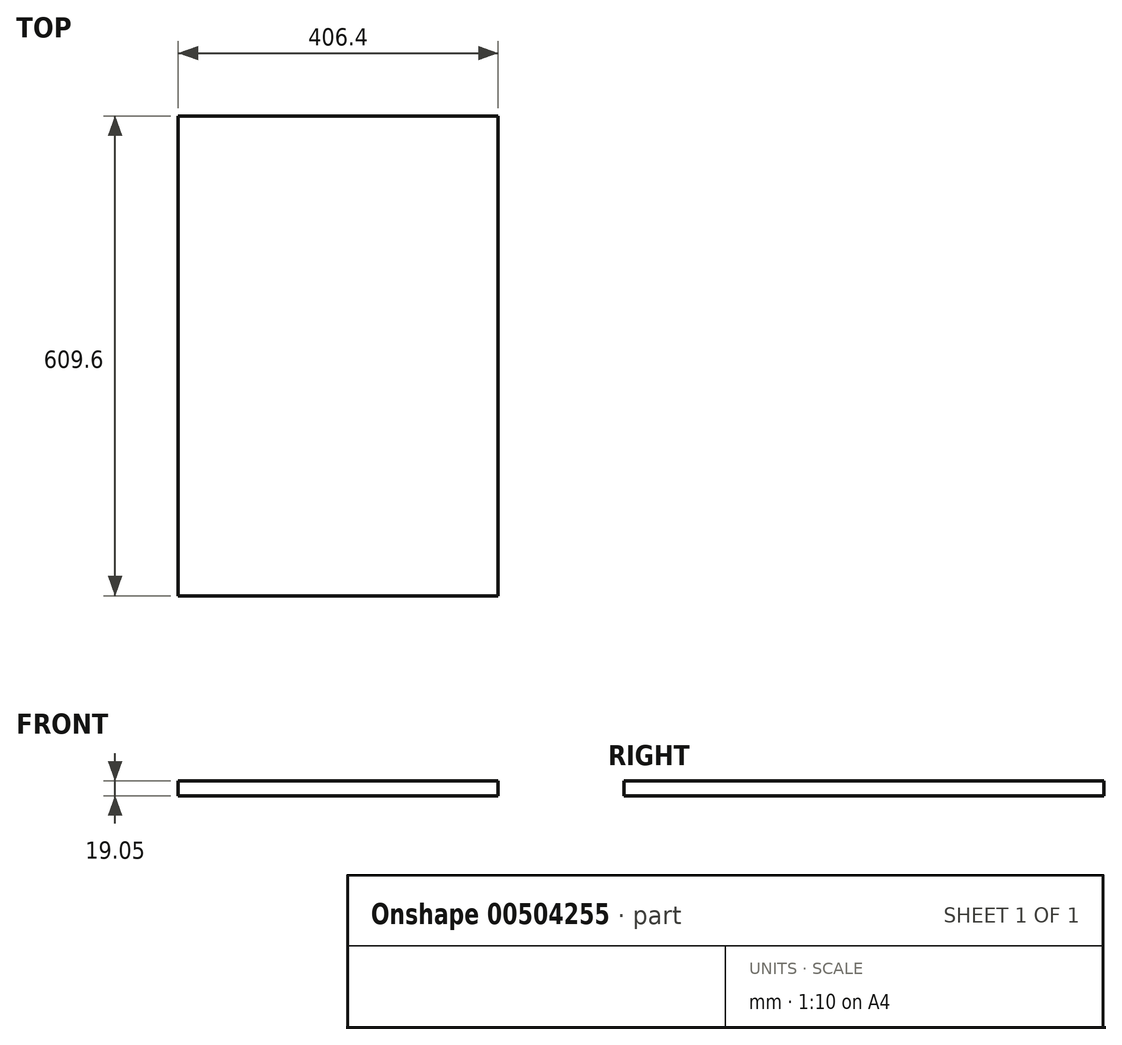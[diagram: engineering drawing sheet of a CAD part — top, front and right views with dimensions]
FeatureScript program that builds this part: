
annotation { "Feature Type Name" : "Feature", "Feature Type Description" : "" }
export const myFeature = defineFeature(function(context is Context, id is Id, definition is map)
    precondition{}
    {
        {
            var Q0;
            Q0=qCreatedBy(makeId("Top.planeOp"),FACE);
            var sketch = newSketch(context, id + "F0", { "sketchPlane" : qUnion([Q0])});
            skLineSegment(sketch, "E0.bottom", {"start": v(203.2, -304.8) * mm, "end": v(-203.2, -304.8) * mm});
            skLineSegment(sketch, "E0.top", {"start": v(203.2, 304.8) * mm, "end": v(-203.2, 304.8) * mm});
            skLineSegment(sketch, "E0.left", {"start": v(203.2, -304.8) * mm, "end": v(203.2, 304.8) * mm});
            skLineSegment(sketch, "E0.right", {"start": v(-203.2, -304.8) * mm, "end": v(-203.2, 304.8) * mm});
            skPoint(sketch, "E0.middle", {"position": v(0, 0) * mm});
            skSolve(sketch);
        }
        {
            var Q0;
            Q0=makeQuery(id+"F0.imprint","IMPRINT",FACE,{"disambiguationData":[TD([[makeQuery(id+"F0.imprint","IMPRINT",EDGE,{"derivedFrom":sQuery(id+"F0.wireOp",EDGE,"E0.bottom")}),-1.0]])]});
            extrude(context, id + "F1", {"entities" : qUnion([Q0]), "depth" : 19.05 * mm});
        }
    });
